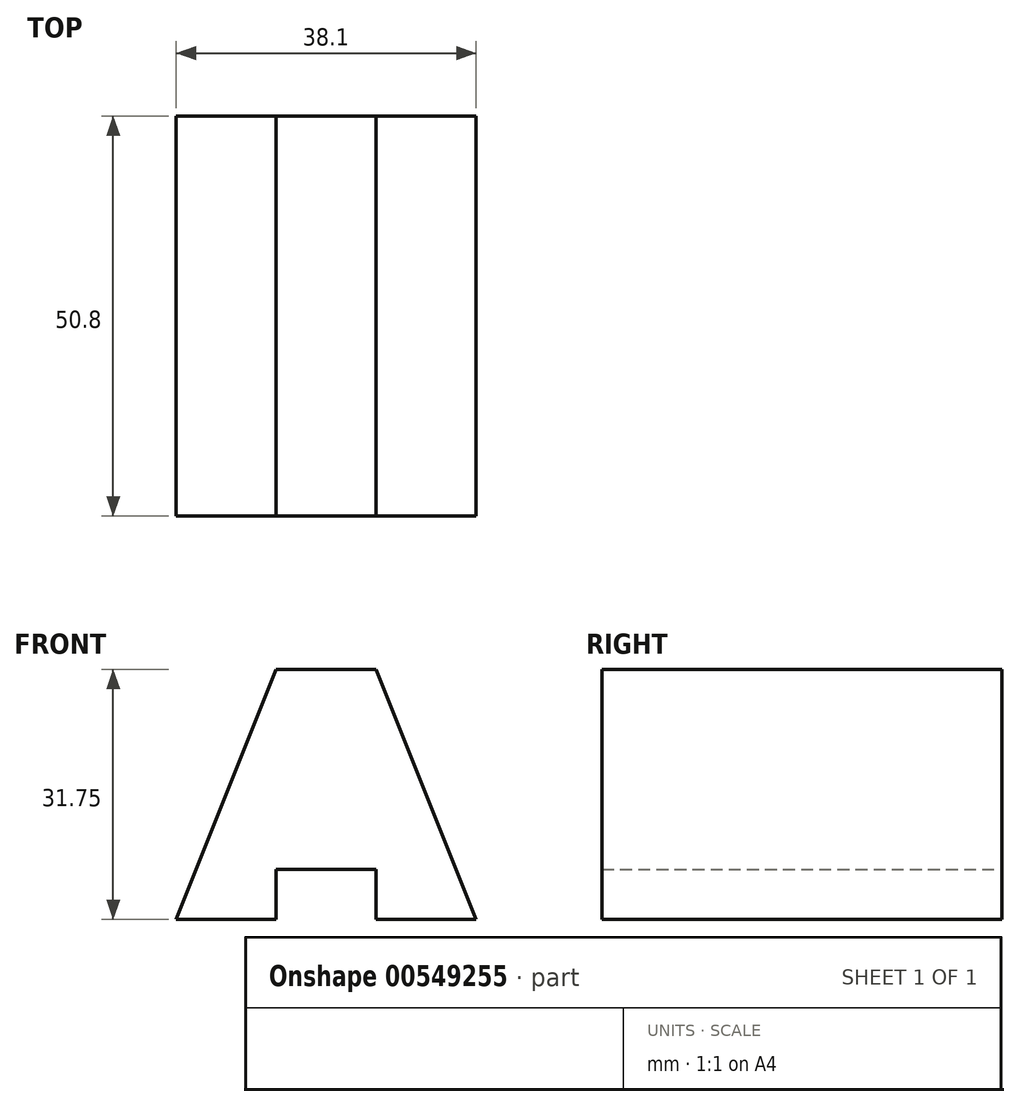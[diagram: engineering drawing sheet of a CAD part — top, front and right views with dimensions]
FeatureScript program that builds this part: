
annotation { "Feature Type Name" : "Feature", "Feature Type Description" : "" }
export const myFeature = defineFeature(function(context is Context, id is Id, definition is map)
    precondition{}
    {
        {
            var Q0;
            Q0=qCreatedBy(makeId("Front.planeOp"),FACE);
            var sketch = newSketch(context, id + "F0", { "sketchPlane" : qUnion([Q0])});
            skLineSegment(sketch, "E0", {"start": v(-62.8, 51.2) * mm, "end": v(-62.8, 19.44) * mm});
            skLineSegment(sketch, "E1", {"start": v(-62.8, 19.44) * mm, "end": v(-50.1, 19.44) * mm});
            skLineSegment(sketch, "E2", {"start": v(-50.1, 19.44) * mm, "end": v(-50.1, 25.8) * mm});
            skLineSegment(sketch, "E3", {"start": v(-50.1, 25.8) * mm, "end": v(-37.4, 25.8) * mm});
            skLineSegment(sketch, "E4", {"start": v(-37.4, 25.8) * mm, "end": v(-37.4, 19.44) * mm});
            skLineSegment(sketch, "E5", {"start": v(-37.4, 19.44) * mm, "end": v(-24.7, 19.44) * mm});
            skLineSegment(sketch, "E6", {"start": v(-24.7, 19.44) * mm, "end": v(-24.7, 51.2) * mm});
            skLineSegment(sketch, "E7", {"start": v(-24.7, 51.2) * mm, "end": v(-62.8, 51.2) * mm});
            skSolve(sketch);
        }
        {
            var Q0;
            Q0 = qSketchRegion(id + "F0", true);
            var Q1;
            Q1 = qSketchRegion(id + "F3", true);
            extrude(context, id + "F1", {"entities" : qUnion([Q0, Q1]), "depth" : 25.4 * mm, "offsetDistance" : 25.4 * mm});
        }
        {
            var Q0;
            Q0=makeQuery(id+"F0.imprint","IMPRINT",FACE,{"disambiguationData":[TD([[makeQuery(id+"F0.imprint","IMPRINT",EDGE,{"derivedFrom":sQuery(id+"F0.wireOp",EDGE,"E0")}),1.0]])]});
            var Q1;
            Q1=makeQuery(id+"F1.opExtrude","CAP_FACE",FACE,{"disambiguationData":[OSD([sQuery(id+"F0.wireOp",EDGE,"E0"),sQuery(id+"F0.wireOp",EDGE,"E1"),sQuery(id+"F0.wireOp",EDGE,"E2"),sQuery(id+"F0.wireOp",EDGE,"E3"),sQuery(id+"F0.wireOp",EDGE,"E4"),sQuery(id+"F0.wireOp",EDGE,"E5"),sQuery(id+"F0.wireOp",EDGE,"E6"),sQuery(id+"F0.wireOp",EDGE,"E7")])],"isStart":false});
            extrude(context, id + "F2", {"entities" : qUnion([Q0, Q1]), "operationType" : NewBodyOperationType.ADD, "depth" : 25.4 * mm, "offsetDistance" : 25.4 * mm});
        }
        {
            var Q0;
            {var subQ0=sQuery(id+"F0.wireOp",EDGE,"E7");var subQ1=sQuery(id+"F0.wireOp",EDGE,"E6");var subQ2=sQuery(id+"F0.wireOp",EDGE,"E5");var subQ3=sQuery(id+"F0.wireOp",EDGE,"E4");var subQ4=sQuery(id+"F0.wireOp",EDGE,"E3");var subQ5=sQuery(id+"F0.wireOp",EDGE,"E2");var subQ6=sQuery(id+"F0.wireOp",EDGE,"E1");var subQ7=sQuery(id+"F0.wireOp",EDGE,"E0");Q0=makeQuery(id+"F2.opExtrude","CAP_FACE",FACE,{"disambiguationData":[OSD([subQ7,subQ6,subQ5,subQ4,subQ3,subQ2,subQ1,subQ0]),TDD([makeQuery(id+"F1.opExtrude","CAP_FACE",FACE,{"disambiguationData":[OSD([subQ7,subQ6,subQ5,subQ4,subQ3,subQ2,subQ1,subQ0])],"isStart":false})])],"isStart":false});}
            var sketch = newSketch(context, id + "F3", { "sketchPlane" : qUnion([Q0])});
            skLineSegment(sketch, "E8", {"start": v(-50.1, 51.2) * mm, "end": v(-62.8, 51.2) * mm});
            skLineSegment(sketch, "E9", {"start": v(-62.8, 51.2) * mm, "end": v(-62.8, 19.44) * mm});
            skLineSegment(sketch, "E10", {"start": v(-62.8, 19.44) * mm, "end": v(-50.1, 51.2) * mm});
            skSolve(sketch);
        }
        {
            var Q0;
            Q0=makeQuery(id+"F3.imprint","IMPRINT",FACE,{"disambiguationData":[TD([[makeQuery(id+"F3.imprint","IMPRINT",EDGE,{"derivedFrom":sQuery(id+"F3.wireOp",EDGE,"E8")}),1.0]])]});
            extrude(context, id + "F4", {"entities" : qUnion([Q0]), "operationType" : NewBodyOperationType.REMOVE, "oppositeDirection" : true, "depth" : 50.8 * mm, "offsetDistance" : 25.4 * mm});
        }
        {
            var Q0;
            {var subQ0=sQuery(id+"F0.wireOp",EDGE,"E7");var subQ1=sQuery(id+"F0.wireOp",EDGE,"E6");var subQ2=sQuery(id+"F0.wireOp",EDGE,"E5");var subQ3=sQuery(id+"F0.wireOp",EDGE,"E4");var subQ4=sQuery(id+"F0.wireOp",EDGE,"E3");var subQ5=sQuery(id+"F0.wireOp",EDGE,"E2");var subQ6=sQuery(id+"F0.wireOp",EDGE,"E1");var subQ7=sQuery(id+"F0.wireOp",EDGE,"E0");Q0=makeQuery(id+"F2.opExtrude","CAP_FACE",FACE,{"disambiguationData":[OSD([subQ7,subQ6,subQ5,subQ4,subQ3,subQ2,subQ1,subQ0]),TDD([makeQuery(id+"F1.opExtrude","CAP_FACE",FACE,{"disambiguationData":[OSD([subQ7,subQ6,subQ5,subQ4,subQ3,subQ2,subQ1,subQ0])],"isStart":false})])],"isStart":false});}
            var sketch = newSketch(context, id + "F5", { "sketchPlane" : qUnion([Q0])});
            skLineSegment(sketch, "E11", {"start": v(-37.4, 51.2) * mm, "end": v(-24.7, 51.2) * mm});
            skLineSegment(sketch, "E12", {"start": v(-24.7, 51.2) * mm, "end": v(-24.7, 19.44) * mm});
            skLineSegment(sketch, "E13", {"start": v(-24.7, 19.44) * mm, "end": v(-37.4, 51.2) * mm});
            skSolve(sketch);
        }
        {
            var Q0;
            Q0 = qSketchRegion(id + "F5", true);
            extrude(context, id + "F6", {"entities" : qUnion([Q0]), "operationType" : NewBodyOperationType.REMOVE, "oppositeDirection" : true, "depth" : 50.8 * mm, "offsetDistance" : 25.4 * mm});
        }
    });
